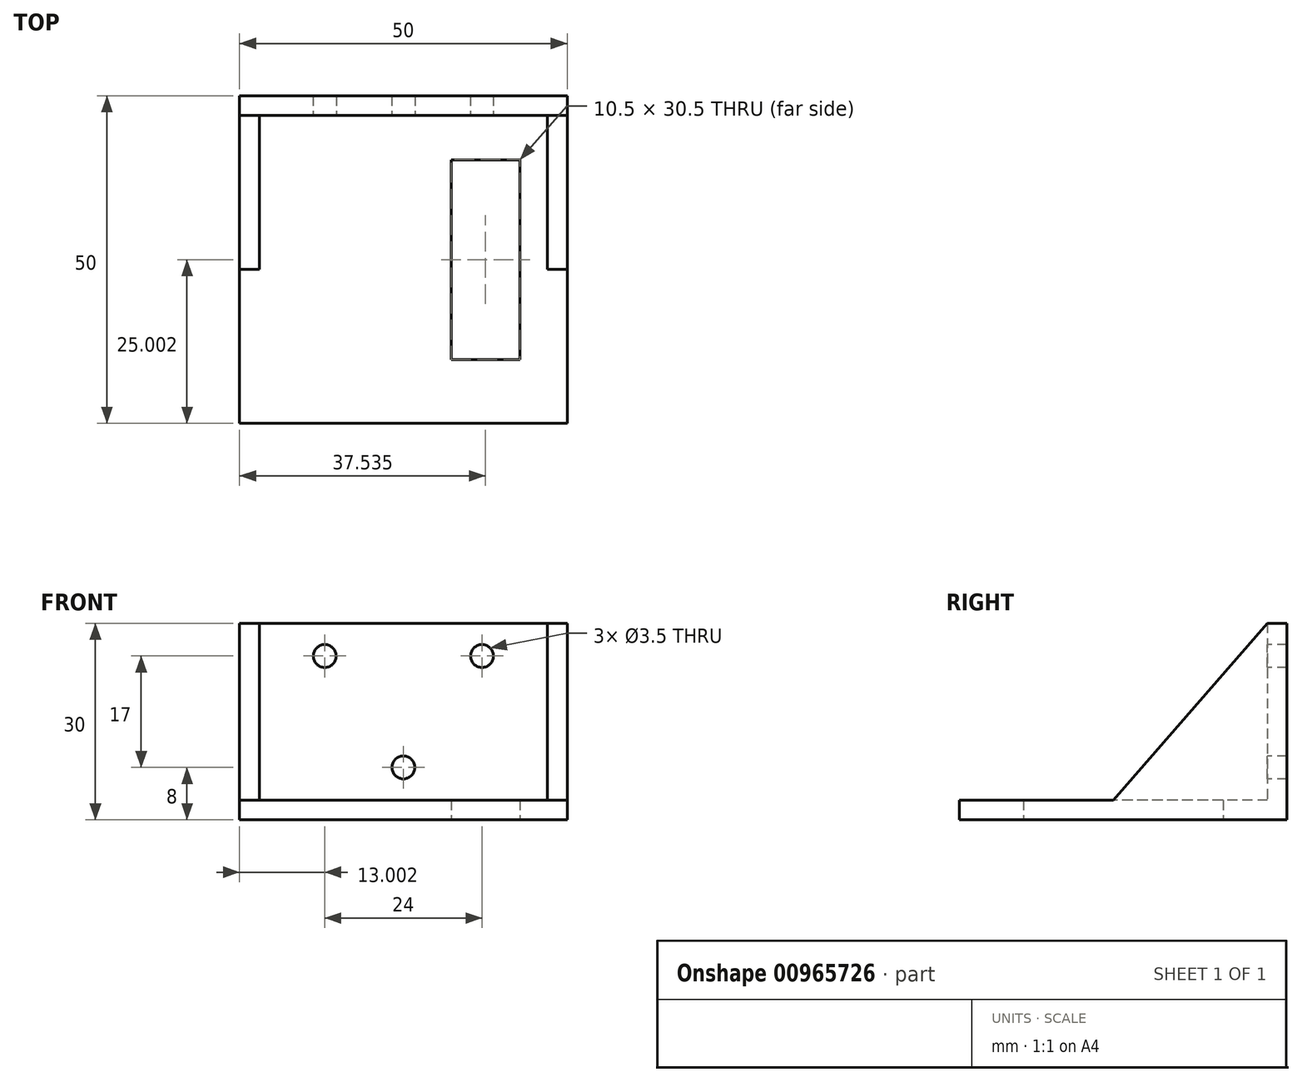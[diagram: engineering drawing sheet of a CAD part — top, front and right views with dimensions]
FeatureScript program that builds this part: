
annotation { "Feature Type Name" : "Feature", "Feature Type Description" : "" }
export const myFeature = defineFeature(function(context is Context, id is Id, definition is map)
    precondition{}
    {
        {
            var Q0;
            Q0=qCreatedBy(makeId("Top.planeOp"),FACE);
            var sketch = newSketch(context, id + "F0", { "sketchPlane" : qUnion([Q0])});
            skLineSegment(sketch, "E0.bottom", {"start": v(-42.9, 27.48) * mm, "end": v(7.1, 27.48) * mm});
            skLineSegment(sketch, "E0.top", {"start": v(-42.9, -22.52) * mm, "end": v(7.1, -22.52) * mm});
            skLineSegment(sketch, "E0.left", {"start": v(-42.9, 27.48) * mm, "end": v(-42.9, -22.52) * mm});
            skLineSegment(sketch, "E0.right", {"start": v(7.1, 27.48) * mm, "end": v(7.1, -22.52) * mm});
            skLineSegment(sketch, "E1", {"start": v(-42.9, 2.48) * mm, "end": v(7.1, 2.48) * mm, "construction": true});
            skLineSegment(sketch, "E2", {"start": v(-17.9, 27.48) * mm, "end": v(-17.9, -22.52) * mm, "construction": true});
            skLineSegment(sketch, "E3", {"start": v(-30.4, 27.48) * mm, "end": v(-30.4, -22.52) * mm, "construction": true});
            skLineSegment(sketch, "E4", {"start": v(-5.4, 27.48) * mm, "end": v(-5.4, -22.52) * mm, "construction": true});
            skLineSegment(sketch, "E5.bottom", {"start": v(-35.68, 17.73) * mm, "end": v(-25.18, 17.73) * mm});
            skLineSegment(sketch, "E5.top", {"start": v(-35.68, -12.77) * mm, "end": v(-25.18, -12.77) * mm});
            skLineSegment(sketch, "E5.left", {"start": v(-35.68, 17.73) * mm, "end": v(-35.68, -12.77) * mm});
            skLineSegment(sketch, "E5.right", {"start": v(-25.18, 17.73) * mm, "end": v(-25.18, -12.77) * mm});
            skLineSegment(sketch, "E6.MirrorCS", {"start": v(-10.61, 17.73) * mm, "end": v(-10.61, -12.77) * mm});
            skLineSegment(sketch, "E7.MirrorCS", {"start": v(-0.11, 17.73) * mm, "end": v(-10.61, 17.73) * mm});
            skLineSegment(sketch, "E8.MirrorCS", {"start": v(-0.11, 17.73) * mm, "end": v(-0.11, -12.77) * mm});
            skLineSegment(sketch, "E9.MirrorCS", {"start": v(-0.11, -12.77) * mm, "end": v(-10.61, -12.77) * mm});
            skLineSegment(sketch, "E10", {"start": v(-42.9, 24.48) * mm, "end": v(7.1, 24.48) * mm});
            skSolve(sketch);
        }
        {
            var Q0;
            {var subQ0=sQuery(id+"F0.wireOp",EDGE,"E0.bottom");Q0=makeQuery(id+"F0.imprint","IMPRINT",FACE,{"disambiguationData":[TD([[makeQuery(id+"F0.imprint","IMPRINT",EDGE,{"derivedFrom":subQ0}),-1.0]])]});}
            extrude(context, id + "F1", {"entities" : qUnion([Q0]), "depth" : 30 * mm, "offsetDistance" : 25 * mm});
        }
        {
            var Q0;
            {var subQ0=sQuery(id+"F0.wireOp",EDGE,"E0.top");Q0=makeQuery(id+"F0.imprint","IMPRINT",FACE,{"disambiguationData":[TD([[makeQuery(id+"F0.imprint","IMPRINT",EDGE,{"derivedFrom":subQ0}),1.0]])]});}
            var Q1;
            Q1=makeQuery(id+"F0.imprint","IMPRINT",FACE,{"disambiguationData":[TD([[makeQuery(id+"F0.imprint","IMPRINT",EDGE,{"derivedFrom":sQuery(id+"F0.wireOp",EDGE,"E5.bottom")}),-1.0]])]});
            extrude(context, id + "F2", {"entities" : qUnion([Q0, Q1]), "operationType" : NewBodyOperationType.ADD, "depth" : 3 * mm, "offsetDistance" : 25 * mm});
        }
        {
            var Q0;
            {var subQ0=sQuery(id+"F0.wireOp",EDGE,"E0.left");Q0=makeQuery(id+"F2.boolean.opBoolean","MERGE",FACE,{"derivedFrom":[makeQuery(id+"F1.opExtrude","SWEPT_FACE",FACE,{"disambiguationData":[OSD([subQ0])]}),makeQuery(id+"F2.opExtrude","SWEPT_FACE",FACE,{"disambiguationData":[OSD([subQ0])]})]});}
            var sketch = newSketch(context, id + "F3", { "sketchPlane" : qUnion([Q0])});
            skLineSegment(sketch, "E11", {"start": v(-24.48, 30) * mm, "end": v(-0.98, 3) * mm});
            skSolve(sketch);
        }
        {
            var Q0;
            {var subQ0=sQuery(id+"F3.wireOp",EDGE,"E11");Q0=makeQuery(id+"F3.imprint","IMPRINT",FACE,{"disambiguationData":[TD([[makeQuery(id+"F3.imprint","IMPRINT",EDGE,{"derivedFrom":subQ0}),-1.0]])]});}
            extrude(context, id + "F4", {"entities" : qUnion([Q0]), "operationType" : NewBodyOperationType.ADD, "oppositeDirection" : true, "depth" : 3 * mm, "offsetDistance" : 25 * mm});
        }
        {
            var Q0;
            {var subQ0=sQuery(id+"F0.wireOp",EDGE,"E0.right");Q0=makeQuery(id+"F2.boolean.opBoolean","MERGE",FACE,{"derivedFrom":[makeQuery(id+"F1.opExtrude","SWEPT_FACE",FACE,{"disambiguationData":[OSD([subQ0])]}),makeQuery(id+"F2.opExtrude","SWEPT_FACE",FACE,{"disambiguationData":[OSD([subQ0])]})]});}
            var sketch = newSketch(context, id + "F5", { "sketchPlane" : qUnion([Q0])});
            skLineSegment(sketch, "E12", {"start": v(24.48, 30) * mm, "end": v(0.98, 3) * mm});
            skSolve(sketch);
        }
        {
            var Q0;
            {var subQ0=sQuery(id+"F5.wireOp",EDGE,"E12");Q0=makeQuery(id+"F5.imprint","IMPRINT",FACE,{"disambiguationData":[TD([[makeQuery(id+"F5.imprint","IMPRINT",EDGE,{"derivedFrom":subQ0}),1.0]])]});}
            extrude(context, id + "F6", {"entities" : qUnion([Q0]), "operationType" : NewBodyOperationType.ADD, "oppositeDirection" : true, "depth" : 3 * mm, "offsetDistance" : 25 * mm});
        }
        {
            var Q0;
            Q0=makeQuery(id+"F1.opExtrude","SWEPT_FACE",FACE,{"disambiguationData":[OSD([sQuery(id+"F0.wireOp",EDGE,"E10")])]});
            var sketch = newSketch(context, id + "F7", { "sketchPlane" : qUnion([Q0])});
            skCircle(sketch, "E13", {"center": v(-29.9, 25) * mm, "radius": 1.75 * mm});
            skCircle(sketch, "E14", {"center": v(-5.9, 25) * mm, "radius": 1.75 * mm});
            skCircle(sketch, "E15", {"center": v(-17.9, 8) * mm, "radius": 1.75 * mm});
            skSolve(sketch);
        }
        {
            var Q0;
            Q0=makeQuery(id+"F7.imprint","IMPRINT",FACE,{"disambiguationData":[TD([[makeQuery(id+"F7.imprint","IMPRINT",EDGE,{"derivedFrom":sQuery(id+"F7.wireOp",EDGE,"E13")}),1.0]])]});
            var Q1;
            Q1=makeQuery(id+"F7.imprint","IMPRINT",FACE,{"disambiguationData":[TD([[makeQuery(id+"F7.imprint","IMPRINT",EDGE,{"derivedFrom":sQuery(id+"F7.wireOp",EDGE,"E14")}),1.0]])]});
            var Q2;
            Q2=makeQuery(id+"F7.imprint","IMPRINT",FACE,{"disambiguationData":[TD([[makeQuery(id+"F7.imprint","IMPRINT",EDGE,{"derivedFrom":sQuery(id+"F7.wireOp",EDGE,"E15")}),1.0]])]});
            extrude(context, id + "F8", {"entities" : qUnion([Q0, Q1, Q2]), "operationType" : NewBodyOperationType.REMOVE, "oppositeDirection" : true, "depth" : 3 * mm, "offsetDistance" : 25 * mm});
        }
    });
